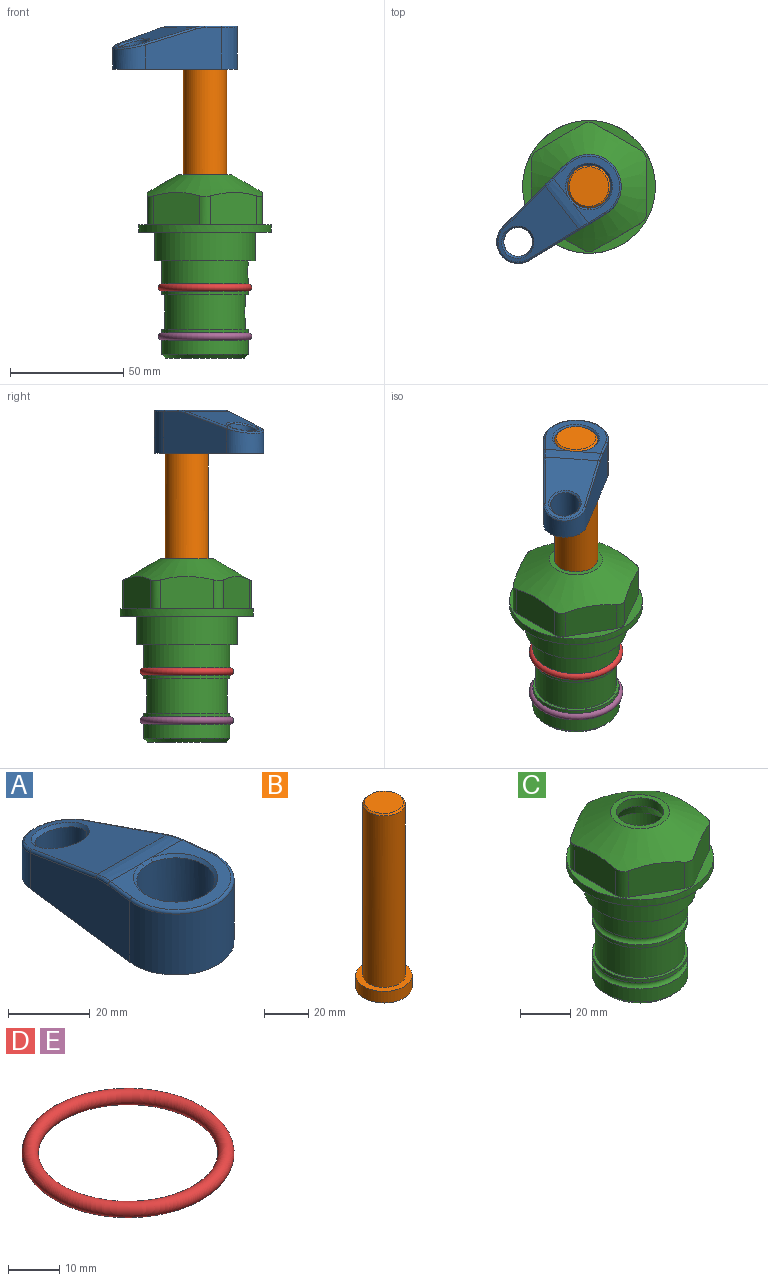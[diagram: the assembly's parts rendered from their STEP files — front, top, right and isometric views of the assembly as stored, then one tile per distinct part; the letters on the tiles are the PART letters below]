
ASSEMBLY  parts=5 mates=4
PART A: 31 faces, bbox 31.7x65.5x19.8 mm
  f0: plane 39.12x18.26mm, normal (0.99,0.12,0), area 612.2mm2, adj f1,f4,f7,f11,f13,f15
  f1: cylinder r=9.53mm len=18.91mm, axis (0,0,-1), area 296.1mm2, adj f0,f2,f7,f17
  f2: plane 39.12x18.26mm, normal (-0.99,0.12,0), area 612.2mm2, adj f1,f4,f7,f12,f14,f16
  f3: cylinder r=6.35mm len=12.7mm, axis (0,0,-1), area 362.4mm2, adj f7,f18
  f4: cylinder r=14.29mm len=28.58mm, axis (0,0,-1), area 882.2mm2, adj f0,f2,f7,f10
  f5: cylinder r=9.53mm len=19.05mm, axis (0,0,-1), area 1092.6mm2, adj f7,f19,f20
  f6: plane 26.99x23.69mm, normal (0,0,1), area 216.2mm2, adj f9,f10,f11,f12,f19
  f7: plane 63.5x28.58mm, normal (0,0,-1), area 661.8mm2, adj f0,f1,f2,f3,f4,f5,f22,f23
  f8: plane 33.52x23.6mm, normal (0,0.26,0.97), area 486mm2, adj f9,f15,f16,f17,f18
  f9: cylinder r=19.05mm len=24.72mm, axis (1,0,0), area 120.4mm2, adj f6,f8,f13,f14,f20
  f10: torus R=13.49mm, axis (0,0,1), area 59mm2, adj f4,f6,f11,f12
  f11: cylinder r=0.79mm len=8.67mm, axis (0.12,-0.99,0), area 10.8mm2, adj f0,f6,f10,f13
  f12: cylinder r=0.79mm len=8.67mm, axis (0.12,0.99,0), area 10.8mm2, adj f2,f6,f10,f14
  f13: bspline ~4.95x1.42mm, area 6.1mm2, adj f0,f9,f11,f15
  f14: bspline ~4.95x1.42mm, area 6.1mm2, adj f2,f9,f12,f16
  f15: cylinder r=0.79mm len=25.95mm, axis (0.12,-0.96,0.26), area 32.9mm2, adj f0,f8,f13,f17
  f16: cylinder r=0.79mm len=25.95mm, axis (0.12,0.96,-0.26), area 32.9mm2, adj f2,f8,f14,f17
  f17: bspline ~18.91x8.38mm, area 30mm2, adj f1,f8,f15,f16
  f18: bspline ~14.29x14.29mm, area 48.3mm2, adj f3,f8
  f19: cone r=9.53mm half-angle=45deg, axis (0,0,1), area 66.5mm2, adj f5,f6,f20
  f20: bspline ~3.22x0.96mm, area 3.5mm2, adj f5,f9,f19
  f21: plane 2.75x2.72mm, normal (0,0,-1), area 2.9mm2, adj f23,f25,f28
  f22: plane 23.05x15.88mm, normal (-0.99,-0.12,0), area 323.6mm2, adj f7,f25,f26,f27,f28,f29
  f23: plane 23.05x15.88mm, normal (0.99,-0.12,0), area 323.6mm2, adj f7,f21,f25,f27,f28,f30
  f24: cylinder r=9.53mm len=10.69mm, axis (0,0,-1), area 114.7mm2, adj f7,f27,f29,f30
  f25: cylinder r=12.7mm len=20.59mm, axis (0,0,-1), area 381.1mm2, adj f7,f21,f22,f23,f26,f28
  f26: plane 2.75x2.72mm, normal (0,0,-1), area 2.9mm2, adj f22,f25,f28
  f27: plane 19.72x18.37mm, normal (0,-0.26,-0.97), area 291.8mm2, adj f22,f23,f24,f28,f29,f30
  f28: cylinder r=15.88mm len=19.92mm, axis (1,0,0), area 54.8mm2, adj f21,f22,f23,f25,f26,f27
  f29: cylinder r=1.59mm len=11mm, axis (0,0,-1), area 34.7mm2, adj f7,f22,f24,f27
  f30: cylinder r=1.59mm len=11mm, axis (0,0,-1), area 34.7mm2, adj f7,f23,f24,f27
PART B: 6 faces, bbox 25.4x25.4x101.6 mm
  f0: plane 17.46x17.46mm, normal (0,0,1), area 239.5mm2, adj f5
  f1: plane 25.4x25.4mm, normal (0,0,-1), area 506.7mm2, adj f2
  f2: cylinder r=12.7mm len=25.4mm, axis (0,0,1), area 506.7mm2, adj f1,f3
  f3: plane 25.4x25.4mm, normal (0,0,1), area 221.7mm2, adj f2,f4
  f4: cylinder r=9.53mm len=94.46mm, axis (0,0,1), area 5653mm2, adj f3,f5
  f5: cone r=8.73mm half-angle=45deg, axis (0,0,-1), area 64.4mm2, adj f0,f4
PART C: 36 faces, bbox 58.7x58.7x81 mm
  f0: cylinder r=17.78mm len=35.56mm, axis (0,0,1), area 1670.8mm2, adj f23,f24,f31
  f1: cylinder r=19.05mm len=38.1mm, axis (0,0,1), area 1191.9mm2, adj f26,f27,f30
  f2: plane 58.66x58.66mm, normal (0,0,-1), area 1150.6mm2, adj f3,f28
  f3: cylinder r=29.33mm len=58.66mm, axis (0,0,-1), area 585.1mm2, adj f2,f4
  f4: plane 58.66x58.66mm, normal (0,0,1), area 475.9mm2, adj f3,f5,f6,f7,f8,f9,f10,f11
  f5: plane 20.32x14.34mm, normal (-0.5,0.87,0), area 324.4mm2, adj f4,f15,f16,f17
  f6: plane 20.32x14.34mm, normal (0.5,0.87,0), area 324.4mm2, adj f4,f14,f15,f17
  f7: plane 23.48x14.34mm, normal (1,0,0), area 324.4mm2, adj f4,f13,f14,f17
  f8: plane 20.32x14.34mm, normal (0.5,-0.87,0), area 324.4mm2, adj f4,f12,f13,f17
  f9: plane 20.32x14.34mm, normal (-0.5,-0.87,0), area 324.4mm2, adj f4,f11,f12,f17
  f10: plane 23.48x14.34mm, normal (-1,0,0), area 324.4mm2, adj f4,f11,f16,f17
  f11: cylinder r=5.08mm len=12.85mm, axis (0,0,-1), area 67.2mm2, adj f4,f9,f10,f17
  f12: cylinder r=5.08mm len=12.85mm, axis (0,0,-1), area 67.2mm2, adj f4,f8,f9,f17
  f13: cylinder r=5.08mm len=12.85mm, axis (0,0,-1), area 67.2mm2, adj f4,f7,f8,f17
  f14: cylinder r=5.08mm len=12.85mm, axis (0,0,-1), area 67.2mm2, adj f4,f6,f7,f17
  f15: cylinder r=5.08mm len=12.85mm, axis (0,0,-1), area 67.2mm2, adj f4,f5,f6,f17
  f16: cylinder r=5.08mm len=12.85mm, axis (0,0,-1), area 67.2mm2, adj f4,f5,f10,f17
  f17: cone r=11.73mm half-angle=60deg, axis (0,0,-1), area 2071.8mm2, adj f5,f6,f7,f8,f9,f10,f11,f12
  f18: plane 23.46x23.46mm, normal (0,0,1), area 147.4mm2, adj f17,f35
  f19: plane 34.93x34.93mm, normal (0,0,-1), area 958mm2, adj f29
  f20: cylinder r=19.05mm len=38.1mm, axis (0,0,1), area 760.1mm2, adj f21,f29
  f21: torus R=19.05mm, axis (0,0,1), area 565.3mm2, adj f20,f22
  f22: cylinder r=19.05mm len=38.1mm, axis (0,0,1), area 190mm2, adj f21,f23
  f23: plane 38.1x38.1mm, normal (0,0,1), area 146.9mm2, adj f0,f22
  f24: plane 38.1x38.1mm, normal (0,0,-1), area 146.9mm2, adj f0,f25
  f25: cylinder r=19.05mm len=38.1mm, axis (0,0,1), area 190mm2, adj f24,f26
  f26: torus R=19.05mm, axis (0,0,1), area 565.3mm2, adj f1,f25
  f27: plane 44.45x44.45mm, normal (0,0,-1), area 411.7mm2, adj f1,f28
  f28: cylinder r=22.23mm len=44.45mm, axis (0,0,1), area 1773.5mm2, adj f2,f27
  f29: cone r=19.05mm half-angle=45deg, axis (0,0,1), area 257.5mm2, adj f19,f20
  f30: cylinder r=3.17mm len=6.75mm, axis (-1,0,0), area 128mm2, adj f1,f33
  f31: cylinder r=3.17mm len=6.35mm, axis (-1,0,0), area 102.5mm2, adj f0,f33
  f32: plane 25.4x25.4mm, normal (0,0,1), area 506.7mm2, adj f33
  f33: cylinder r=12.7mm len=66.42mm, axis (0,0,-1), area 5236.2mm2, adj f30,f31,f32,f34
  f34: cone r=9.53mm half-angle=30deg, axis (0,0,-1), area 443.4mm2, adj f33,f35
  f35: cylinder r=9.53mm len=19.05mm, axis (0,0,-1), area 240.9mm2, adj f18,f34
PART D: 1 faces, bbox 44.7x44.7x3.2 mm
  f0: torus R=19.05mm, axis (0,0,1), area 1193.9mm2
PART E: same geometry as D
PLACE A rot(axis=(0,0,1),128deg) t=(0,0,27.55)mm
PLACE B rot(axis=(0,0,-1),138.7deg) t=(0,0,27.55)mm
PLACE C at identity fixed
PLACE D at identity
PLACE E t=(0,0,-21.59)mm
MATE fastened D.f0 <-> C.f0  axis (0,0,1) through (0,0,-24.51)mm
MATE cylindrical B.f2 <-> C.f0  axis (0,0,-1) through (0,0,-10.55)mm
MATE revolute B.f2 <-> A.f4  axis (0,0,1) through (0,0,91.05)mm
MATE fastened C.f0 <-> E.f0  axis (0,0,1) through (0,0,-46.1)mm
